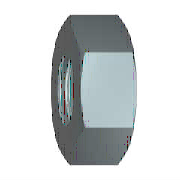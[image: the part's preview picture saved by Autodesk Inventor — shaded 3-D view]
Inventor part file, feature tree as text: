
AUTODESK INVENTOR PART (.ipt)
format: ipt  version: 2022 (Build 260153000, 153)  size: 164,864 bytes
history: native  units: mm (DEFAULTED — no unit token found)
features: sketch x3, chamfer x1, hole x1, other x1, plane x1
ambient origin geometry x7: Origin, YZ Plane, XZ Plane, X Axis, Y Axis, Z Axis, Center Point
bodies: Solid1 (feature_tree), Body (feature_tree)
feature tree (7):
  chamfer  "Chamfer1"  Angle=30.0deg  [1 undecoded]
  hole  "Thread"  [1 undecoded]
  other  "Work Axis1"
  plane  "Work Plane1"
  sketch  "Sketch1"  dims[d0=11.547005mm]
  sketch  "Sketch2"  dims[d1=5.2mm]
  sketch  "Sketch3"  dims[d2=0.0mm d3=30.0deg d4=30.0deg d5=8.9mm d6=8.9mm d7=90.0deg d25=4.917mm d26=6.0mm d27=4.0mm d28=2.0mm d29=14.3117mm d30=8.0mm d31=20.594885mm d8=0.541266mm d9=30.0deg d10=0.541266mm d11=30.0deg d13=0.0mm d14=0.0mm d39=0.0mm d40=0.541266mm d41=0.541266mm d42=0.0mm]
note: 2 required parameter values undecoded (feature->parameter linkage not recoverable at this tier; creation-order binding heuristic only, values carry confidence <= 0.55)
